# Revit family: BC_Hitachi_Air-365-Max_LOD400
name_source: partatom
category: Equipement de génie climatique
revit_build: Autodesk Revit 2018 (Build: 20170223_1515(x64)
units: mm (PartAtom-declared; Revit-internal decimal feet)

## family parameters
Basée sur le plan de construction = Non
Classification = Aucun
Cote de connecteur circulaire = Utiliser le diamètre
Couper avec des vides une fois chargée = Non
Partagée = Non
Point de calcul de pièce = Non
Toujours verticalement = Oui
Type d'élément = Normal

## types (9) — shared parameters
BC_MODEL_ID = 1040496
BC_OBJECT_ID = 317346
BC_OBJECT_VERSION = #6
Color = L*=79.39, a*=0.00, b*=4.69*
Compressor type = Hermetic (vapor-injection scroll compressor )
Description = Heat pump and Heat recovery modular top flow outdoors
Frequency = 50 Hz
Manufacturer = Hitachi Air Conditioning Europe SAS
MasterFormat = Split-System Air-Conditioners
Masterformat Code = 23 81 26
Modèle = Air 365 Max
Name BIM&CO = Outdoor Unit
Nominal Voltage = 400 V
Number of Poles = 3
OmniClass code = 23-33 39 11
OmniClass description = Air Conditioners
Overall depth = 770 mm  [stored 2.52625 ft]
Overall height = 1793 mm  [stored 5.88255 ft]
Refrigerant Type = R410a
Uniformat = Distribution Systems
Uniformat code = D3040

## per-type parameters (varying)
| type | BC_VARIANT_ID | Coefficient of Performance (COP) | Diameter 1 | Energy efficiency ratio (EER) | Gross Weight | High Pressure Gas Diameter | Liquid Diameter | Liquid pipe (inch) | Low Pressure Gas Diameter | Mass | Nominal Cooling Capacity | Nominal Current | Nominal Heating Capacity | Outlet offset | Overall width | Product Code | Reference description | Second outlet | Sound Power (Cooling) | Sound Power (Heating) | Void offset H | Void offset V |
| RAS-8FSXNS2E | 783692 | 4.62 | Oui | 3.57 | 203.00 kg | 16 mm | 10 mm  [stored 0.0328084 ft] | 3/8 | 19 mm | 197.00 kg | 22400 W | 16 A | 22400 W | 0 mm  [stored 0 ft] | 948 mm  [stored 3.11024 ft] | 7E335010 | OU Top Flow HP / HR 8,0 HP (22,4 kW) 400V/3 phase | Non | 77 | 78 | 0 mm  [stored 0 ft] | 12 mm  [stored 0.0393701 ft] |
| RAS-10FSXNS2E | 783693 | 4.34 | Oui | 3.41 | 208.00 kg | 19 mm | 10 mm  [stored 0.0328084 ft] | 3/8 | 22 mm | 203.00 kg | 28000 W | 20 A | 28000 W | 0 mm  [stored 0 ft] | 948 mm  [stored 3.11024 ft] | 7E335011 | OU Top Flow HP / HR 10,0 HP (28,0 kW) 400V/3 phase | Non | 79 | 80 | 0 mm  [stored 0 ft] | 12 mm  [stored 0.0393701 ft] |
| RAS-12FSXNS2E | 783709 | 3.34 | Oui | 3.21 | 225.00 kg | 22 mm | 13 mm | 1/2 | 25 mm  [stored 0.082021 ft] | 217.00 kg | 33500 W | 23 A | 33500 W | 0 mm  [stored 0 ft] | 948 mm  [stored 3.11024 ft] | 7E335012 | OU Top Flow HP / HR 12,0 HP (33,5 kW) 400V/3 phase | Non | 82 | 83 | 0 mm  [stored 0 ft] | 12 mm  [stored 0.0393701 ft] |
| RAS-14FSXNS2E | 783710 | 3.86 | Non | 2.52 | 280.00 kg | 22 mm | 13 mm | 1/2 | 25 mm  [stored 0.082021 ft] | 271.00 kg | 40000 W | 28 A | 40000 W | 302 mm  [stored 0.990814 ft] | 1208 mm  [stored 3.96325 ft] | 7E335030 | OU Top Flow HP / HR 14,0 HP (40,0 kW) 400V/3 phase | Oui | 81 | 80 | 0 mm  [stored 0 ft] | 12 mm  [stored 0.0393701 ft] |
| RAS-16FSXNS2E | 783711 | 4.04 | Non | 2.64 | 281.00 kg | 22 mm | 13 mm | 1/2 | 29 mm | 272.00 kg | 45000 W | 33 A | 45000 W | 302 mm  [stored 0.990814 ft] | 1208 mm  [stored 3.96325 ft] | 7E335031 | OU Top Flow HP / HR 16,0 HP (45,0 kW) 400V/3 phase | Oui | 83 | 82 | 0 mm  [stored 0 ft] | 12 mm  [stored 0.0393701 ft] |
| RAS-18FSXNS2E | 783712 | 3 | Non | 2.84 | 281.00 kg | 22 mm | 16 mm | 5/8 | 29 mm | 272.00 kg | 50000 W | 40 A | 50000 W | 302 mm  [stored 0.990814 ft] | 1208 mm  [stored 3.96325 ft] | 7E335032 | OU Top Flow HP / HR 18,0 HP (50,0 kW) 400V/3 phase | Oui | 85 | 86 | 0 mm  [stored 0 ft] | 12 mm  [stored 0.0393701 ft] |
| RAS-20FSXNS2E | 783713 | 3.5 | Oui | 2.84 | 361.00 kg | 22 mm | 16 mm | 5/8 | 29 mm | 350.00 kg | 56000 W | 40 A | 56000 W | 400 mm | 1598 mm  [stored 5.24278 ft] | 7E335039 | OU Top Flow HP / HR 20,0 HP (56,0 kW) 400V/3 phase | Oui | 84 | 85 | 365 mm | 0 mm  [stored 0 ft] |
| RAS-22FSXNS2E | 783714 | 3.36 | Oui | 2.73 | 361.00 kg | 25 mm  [stored 0.082021 ft] | 16 mm | 5/8 | 29 mm | 350.00 kg | 61500 W | 43 A | 61500 W | 400 mm | 1598 mm  [stored 5.24278 ft] | 7E335051 | OU Top Flow HP / HR 22,0 HP (61,5 kW) 400V/3 phase | Oui | 84 | 85 | 365 mm | 0 mm  [stored 0 ft] |
| RAS-24FSXNS2E | 783715 | 3.47 | Oui | 2.72 | 386.00 kg | 25 mm  [stored 0.082021 ft] | 16 mm | 5/8 | 29 mm | 350.00 kg | 67000 W | 53 A | 67000 W | 400 mm | 1598 mm  [stored 5.24278 ft] | 7E335040 | OU Top Flow HP / HR 24,0 HP (67,0 kW) 400V/3 phase | Oui | 85 | 86 | 365 mm | 0 mm  [stored 0 ft] |

note: column(s) folded — value = type name in every type: Reference

note: [stored X ft] marks values corroborated as IEEE doubles in the binary element streams (Revit-internal decimal feet)
